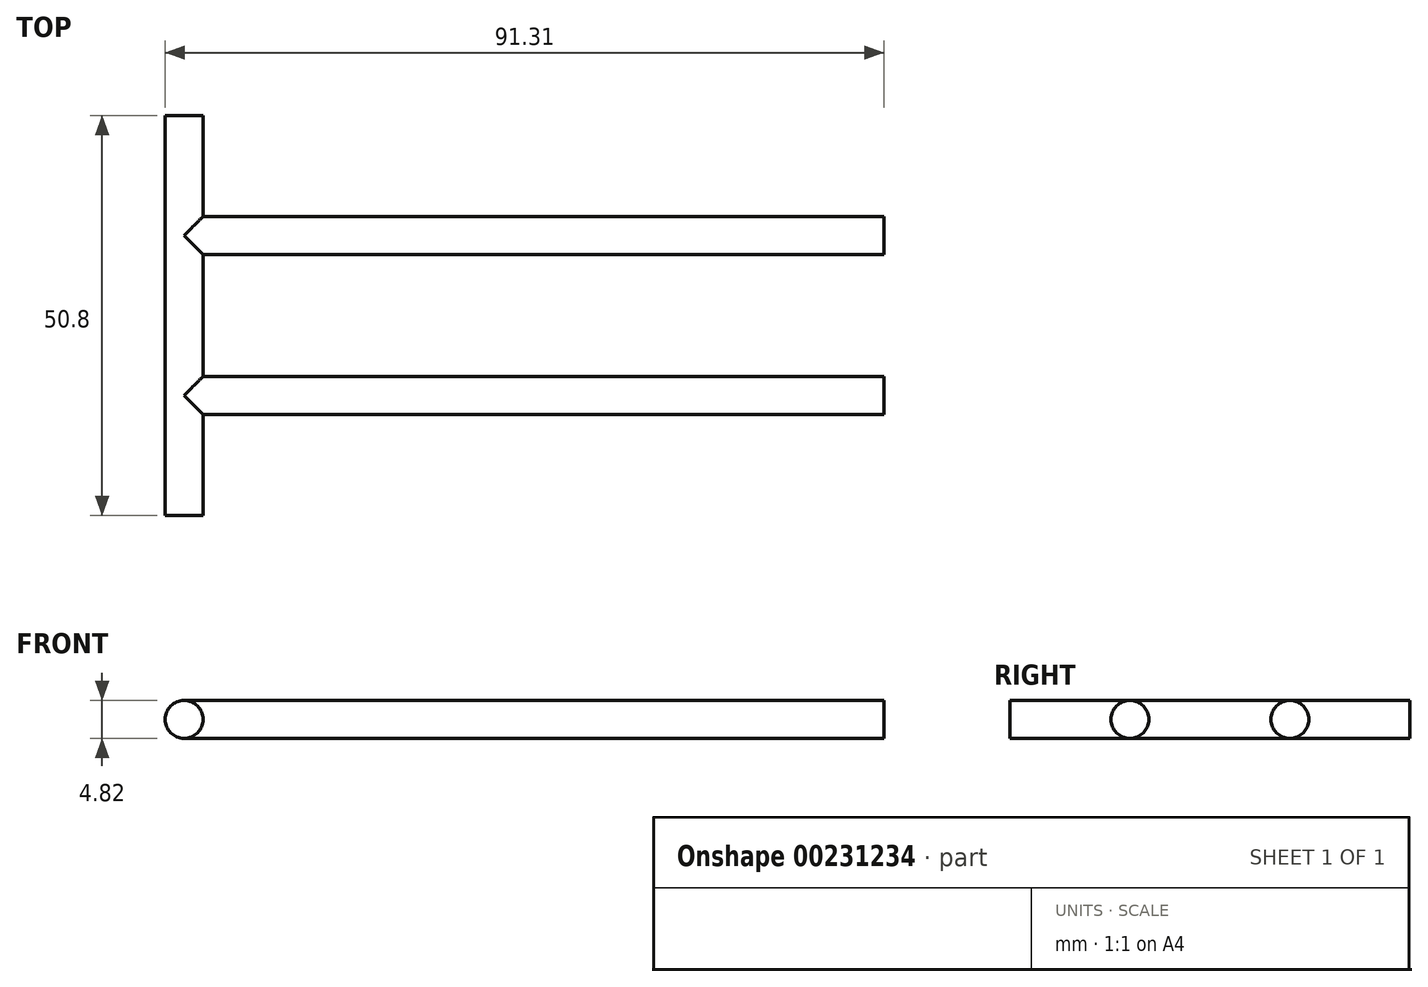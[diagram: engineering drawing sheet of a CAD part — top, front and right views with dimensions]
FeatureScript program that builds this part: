
annotation { "Feature Type Name" : "Feature", "Feature Type Description" : "" }
export const myFeature = defineFeature(function(context is Context, id is Id, definition is map)
    precondition{}
    {
        {
            var Q0;
            Q0=qCreatedBy(makeId("Front.planeOp"),FACE);
            var sketch = newSketch(context, id + "F0", { "sketchPlane" : qUnion([Q0])});
            skCircle(sketch, "E0", {"center": v(0, 0) * mm, "radius": 2.41 * mm});
            skSolve(sketch);
        }
        {
            var Q0;
            Q0=makeQuery(id+"F0.imprint","IMPRINT",FACE,{"disambiguationData":[TD([[makeQuery(id+"F0.imprint","IMPRINT",EDGE,{"derivedFrom":sQuery(id+"F0.wireOp",EDGE,"E0")}),1.0]])]});
            extrude(context, id + "F1", {"entities" : qUnion([Q0]), "depth" : 50.8 * mm});
        }
        {
            var Q0;
            Q0=qCreatedBy(makeId("Right.planeOp"),FACE);
            var sketch = newSketch(context, id + "F2", { "sketchPlane" : qUnion([Q0])});
            skPoint(sketch, "E1", {"position": v(0, 0) * mm});
            skPoint(sketch, "E2", {"position": v(-35.56, 2.41) * mm});
            skPoint(sketch, "E3", {"position": v(-15.24, 2.41) * mm});
            skPoint(sketch, "E4", {"position": v(-15.24, 0) * mm});
            skPoint(sketch, "E5", {"position": v(-35.56, 0) * mm});
            skCircle(sketch, "E6", {"center": v(-35.56, 0) * mm, "radius": 2.41 * mm});
            skCircle(sketch, "E7", {"center": v(-15.24, 0) * mm, "radius": 2.41 * mm});
            skSolve(sketch);
        }
        {
            var Q0;
            Q0 = qSketchRegion(id + "F2", true);
            extrude(context, id + "F3", {"entities" : qUnion([Q0]), "operationType" : NewBodyOperationType.ADD, "depth" : 88.9 * mm});
        }
    });
